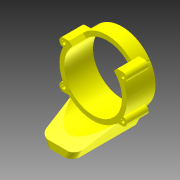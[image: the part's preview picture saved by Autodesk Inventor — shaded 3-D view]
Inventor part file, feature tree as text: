
AUTODESK INVENTOR PART (.ipt)
format: ipt  version: 2012 (Build 160160000, 160)  size: 229,888 bytes
history: native  units: in
note: dims shown in document units (in); Inventor stores cm internally (conversion verified against a paired STEP export)
features: extrude x6, sketch x3, projected_geometry x2, plane x1, fillet x1
ambient origin geometry x8: Origin, YZ Plane, XZ Plane, XY Plane, X Axis, Y Axis, Z Axis, Center Point
bodies: Solid1 (feature_tree)
feature tree (13):
  sketch  "Sketch1"  dims[d0=2.518in d1=0.3in d2=0.134in d3=0.6875in d4=0.3in d5=0.134in d6=0.3in d7=0.134in d8=0.3in d9=0.134in d10=2.3998in d11=2.0638in d12=0.0575in d14=1.0in]
  extrude  "Extrusion1"  Depth=1.0in
  extrude  "Extrusion2"  Depth=1.03in TaperAngle=0.0deg
  extrude  "Extrusion3"  Depth=0.5in TaperAngle=0.0deg
  extrude  "Extrusion4"  Depth=1.25in TaperAngle=0.0deg
  extrude  "Extrusion5"  Depth=0.25in TaperAngle=0.0deg
  plane  "Work Plane1"
  extrude  "Extrusion6"  [1 undecoded]
  fillet  "Fillet1"  Radius=0.25in
  sketch  "Sketch2"  dims[d15=0.5in d16=1.03in d17=0.0in]
  projected_geometry  "Projected Loop1"
  sketch  "Sketch3"  dims[d18=1.03in d19=0.0in d20=0.5in d21=0.0in d22=1.25in d23=0.0in d24=0.25in d25=0.0in d26=-1.25in d27=0.25in d28=0.0625in d29=0.25in d30=0.0in d31=0.75in d32=0.25in d33=1.0547in]
  projected_geometry  "Projected Loop2"
note: 1 required parameter value undecoded (feature->parameter linkage not recoverable at this tier; creation-order binding heuristic only, values carry confidence <= 0.55)
